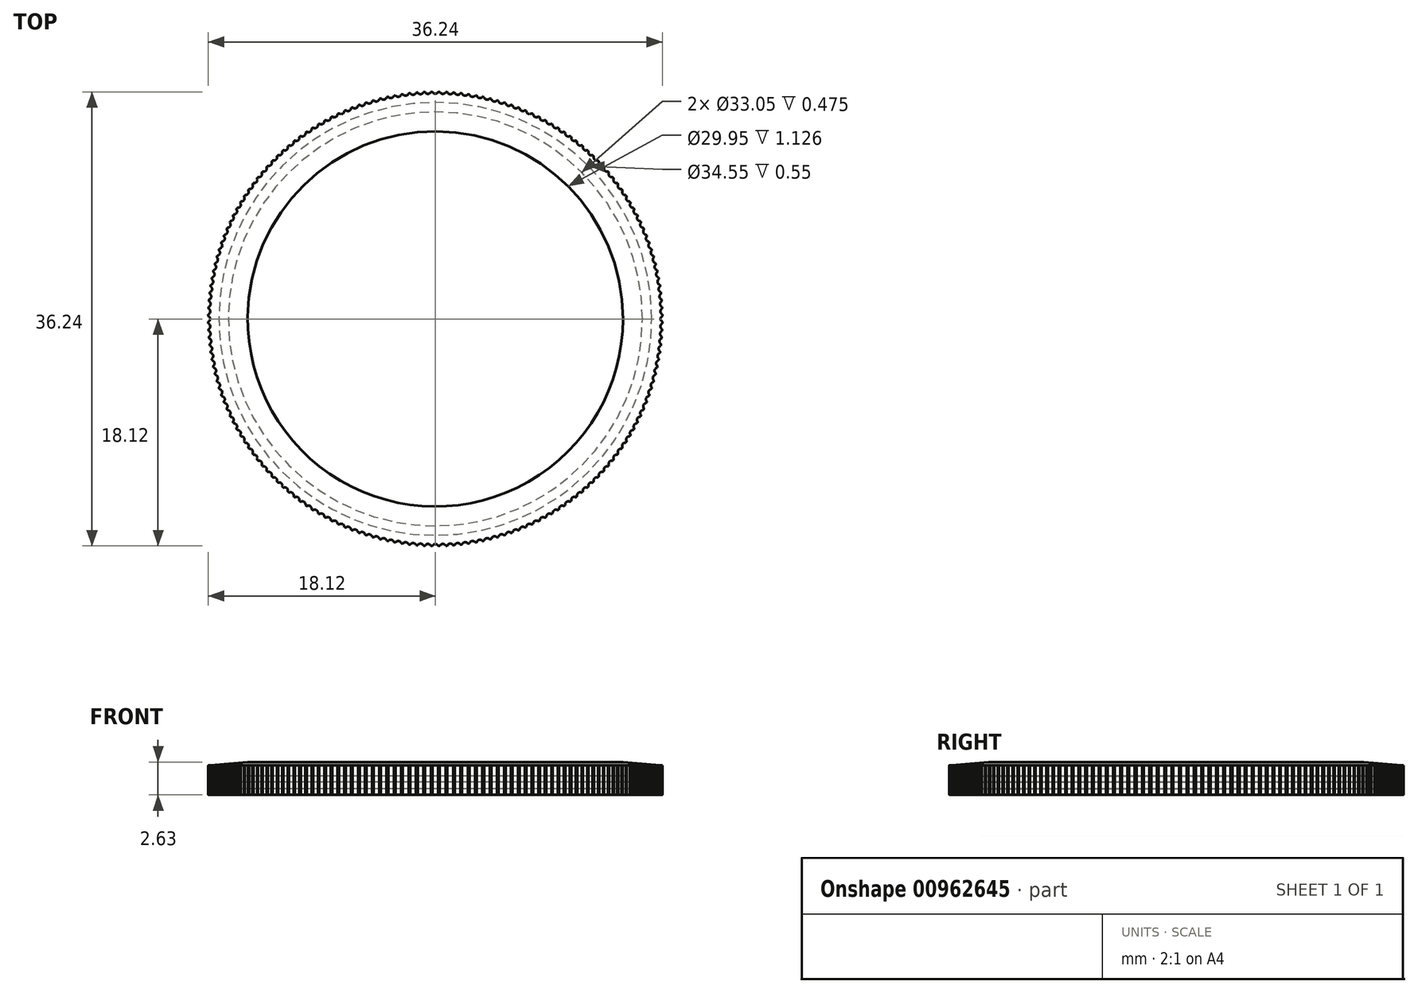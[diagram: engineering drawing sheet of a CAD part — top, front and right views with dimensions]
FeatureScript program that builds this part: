
annotation { "Feature Type Name" : "Feature", "Feature Type Description" : "" }
export const myFeature = defineFeature(function(context is Context, id is Id, definition is map)
    precondition{}
    {
        {
            assignVariable(context, id + "F0", {"name" : "dIn", "anyValue" : 31.5 * mm});
        }
        {
            assignVariable(context, id + "F1", {"name" : "dOut", "anyValue" : getVariable(context, 'dIn') + 3.15 * mm});
        }
        {
            assignVariable(context, id + "F2", {"name" : "bevel", "anyValue" : 5 * degree});
        }
        {
            assignVariable(context, id + "F3", {"name" : "hOut", "anyValue" : 2.35 * mm});
        }
        {
            assignVariable(context, id + "F4", {"name" : "hIn", "anyValue" : getVariable(context, 'hOut') + (getVariable(context, 'dOut') - getVariable(context, 'dIn')) * tan(getVariable(context, 'bevel'))});
        }
        {
            assignVariable(context, id + "F5", {"name" : "hMid", "anyValue" : 1.5 * mm});
        }
        {
            var Q0;
            Q0=qCreatedBy(makeId("Top.planeOp"),FACE);
            var sketch = newSketch(context, id + "F6", { "sketchPlane" : qUnion([Q0])});
            skCircle(sketch, "E0", {"center": v(0, 0) * mm, "radius": 16.53 * mm});
            skSolve(sketch);
        }
        {
            var Q0;
            Q0=qCreatedBy(makeId("Front.planeOp"),FACE);
            var sketch = newSketch(context, id + "F7", { "sketchPlane" : qUnion([Q0])});
            skLineSegment(sketch, "E1.0", {"start": v(-16.53, 0) * mm, "end": v(16.53, 0) * mm, "construction": true});
            skLineSegment(sketch, "E2", {"start": v(16.53, 0) * mm, "end": v(16.53, -0.48) * mm});
            skLineSegment(sketch, "E3", {"start": v(16.53, -0.47) * mm, "end": v(17.28, -0.47) * mm});
            skLineSegment(sketch, "E4", {"start": v(17.28, -0.48) * mm, "end": v(17.28, -1.03) * mm});
            skLineSegment(sketch, "E5", {"start": v(17.28, -1.03) * mm, "end": v(16.53, -1.03) * mm});
            skLineSegment(sketch, "E6", {"start": v(16.53, -1.02) * mm, "end": v(16.53, -1.5) * mm});
            skLineSegment(sketch, "E7", {"start": v(16.53, -1.5) * mm, "end": v(18.12, -1.5) * mm});
            skLineSegment(sketch, "E8", {"start": v(18.12, -1.5) * mm, "end": v(18.12, 0.85) * mm});
            skLineSegment(sketch, "E9", {"start": v(18.12, 0.85) * mm, "end": v(14.97, 1.13) * mm});
            skLineSegment(sketch, "E10", {"start": v(14.97, 1.13) * mm, "end": v(14.97, 0) * mm});
            skLineSegment(sketch, "E11", {"start": v(14.97, 0) * mm, "end": v(16.53, 0) * mm});
            skLineSegment(sketch, "E12", {"start": v(0, 5) * mm, "end": v(0, -5) * mm, "construction": true});
            skSolve(sketch);
        }
        {
            var Q0;
            Q0 = qSketchRegion(id + "F7", true);
            var Q1;
            Q1=sQuery(id+"F6.wireOp",EDGE,"E0");
            sweep(context, id + "F8", {"profiles" : qUnion([Q0]), "path" : qUnion([Q1])});
        }
        {
            var Q0;
            Q0=qCreatedBy(makeId("Top.planeOp"),FACE);
            var sketch = newSketch(context, id + "F9", { "sketchPlane" : qUnion([Q0])});
            skCircle(sketch, "E13", {"center": v(18.22, 0) * mm, "radius": 0.25 * mm});
            skSolve(sketch);
        }
        {
            var Q0;
            Q0 = qSketchRegion(id + "F9", true);
            extrude(context, id + "F10", {"entities" : qUnion([Q0]), "depth" : getVariable(context, 'hIn') - getVariable(context, 'hMid'), "offsetDistance" : 25 * mm, "hasSecondDirection" : true, "secondDirectionOppositeDirection" : true, "secondDirectionDepth" : getVariable(context, 'hMid')});
        }
        {
            var Q0;
            Q0=makeQuery(id+"F10.opExtrude","SWEPT_BODY",BODY,{"disambiguationData":[OSD([sQuery(id+"F9.wireOp",EDGE,"E13")])]});
            var Q1;
            Q1=sQuery(id+"F7.wireOp",EDGE,"E12");
            circularPattern(context, id + "F11", {"operationType" : NewBodyOperationType.REMOVE, "entities" : qUnion([Q0]), "axis" : qUnion([Q1]), "angle" : 360 * degree, "instanceCount" : 192, "equalSpace" : true});
        }
    });
